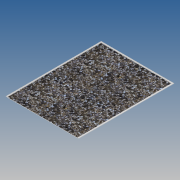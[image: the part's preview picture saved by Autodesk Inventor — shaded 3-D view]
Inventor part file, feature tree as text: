
AUTODESK INVENTOR PART (.ipt)
format: ipt  version: 2020 (Build 240168000, 168)  size: 118,784 bytes
history: native  units: mm
features: extrude x2, sketch x2
ambient origin geometry x8: Origin, YZ Plane, XZ Plane, XY Plane, X Axis, Y Axis, Z Axis, Center Point
bodies: Solid1 (feature_tree)
feature tree (4):
  extrude  "Extrusion1"  Depth=400.0mm
  extrude  "Extrusion2"  Depth=5.0mm
  sketch  "Sketch1"  dims[d0=300.0mm d1=400.0mm]
  sketch  "Sketch2"  dims[d2=1.0mm d3=0.0mm d4=5.0mm d5=405.0mm d6=5.0mm d7=405.0mm d8=1.0mm d9=0.0mm]
